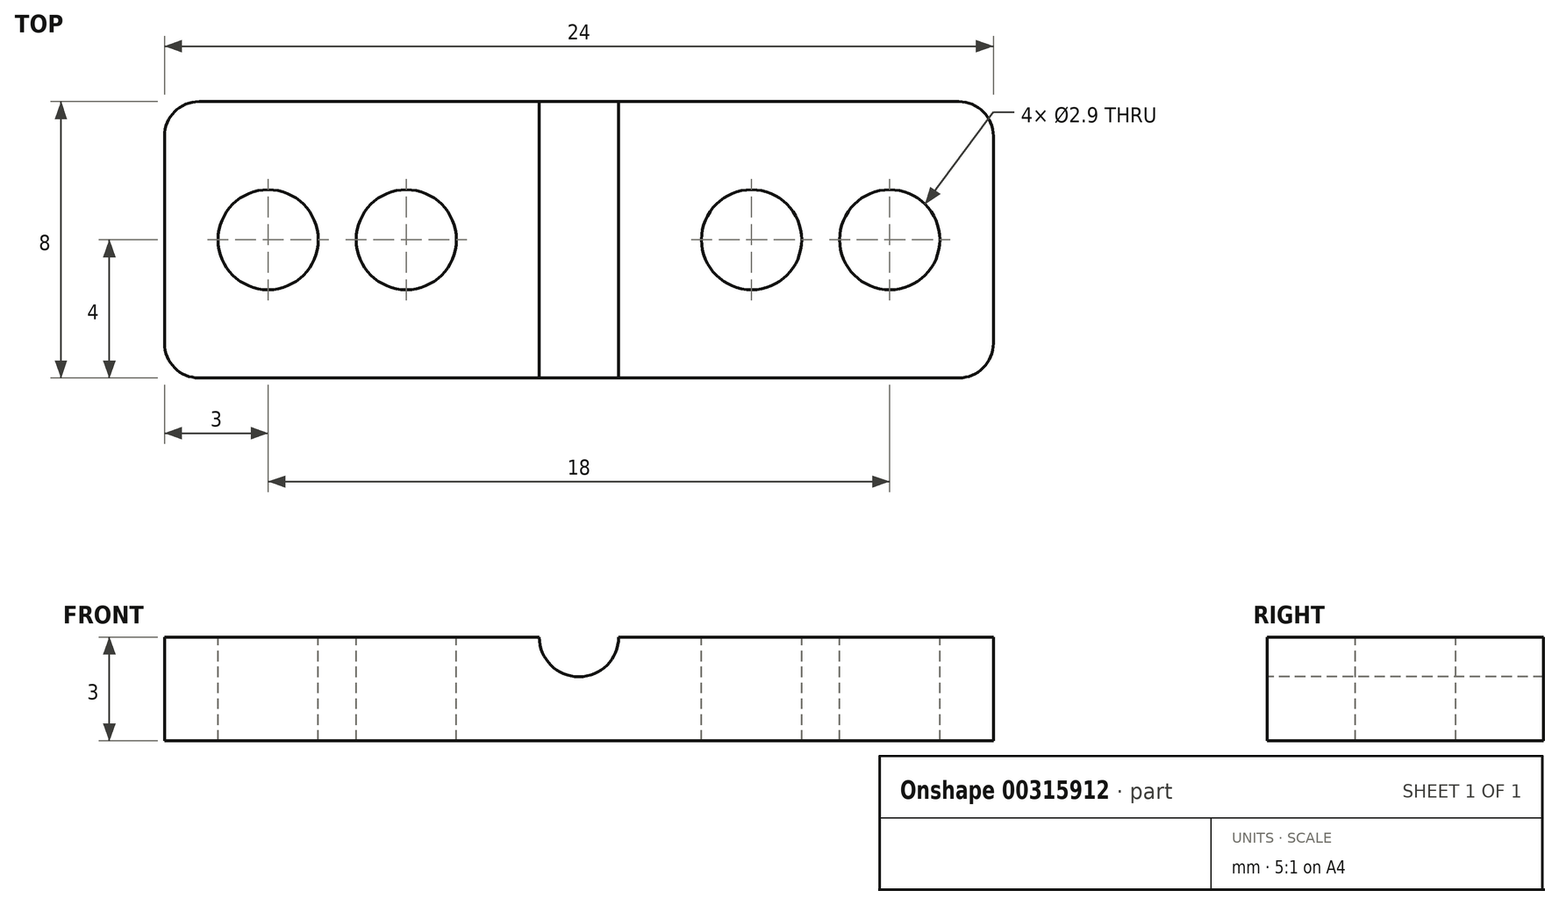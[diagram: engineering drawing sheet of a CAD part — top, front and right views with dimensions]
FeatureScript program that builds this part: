
annotation { "Feature Type Name" : "Feature", "Feature Type Description" : "" }
export const myFeature = defineFeature(function(context is Context, id is Id, definition is map)
    precondition{}
    {
        {
            var Q0;
            Q0=qCreatedBy(makeId("Top.planeOp"),FACE);
            var sketch = newSketch(context, id + "F0", { "sketchPlane" : qUnion([Q0])});
            skLineSegment(sketch, "E0.bottom", {"start": v(3, 4) * mm, "end": v(-3, 4) * mm});
            skLineSegment(sketch, "E0.top", {"start": v(3, -4) * mm, "end": v(-3, -4) * mm});
            skLineSegment(sketch, "E0.left", {"start": v(3, 4) * mm, "end": v(3, -4) * mm});
            skLineSegment(sketch, "E0.right", {"start": v(-3, 4) * mm, "end": v(-3, -4) * mm});
            skPoint(sketch, "E0.middle", {"position": v(0, 0) * mm});
            skLineSegment(sketch, "E1.bottom", {"start": v(21, 4) * mm, "end": v(15, 4) * mm});
            skLineSegment(sketch, "E1.top", {"start": v(21, -4) * mm, "end": v(15, -4) * mm});
            skLineSegment(sketch, "E1.left", {"start": v(21, 4) * mm, "end": v(21, -4) * mm});
            skLineSegment(sketch, "E1.right", {"start": v(15, 4) * mm, "end": v(15, -4) * mm});
            skPoint(sketch, "E1.middle", {"position": v(18, 0) * mm});
            skLineSegment(sketch, "E2", {"start": v(3, 4) * mm, "end": v(15, 4) * mm});
            skLineSegment(sketch, "E3", {"start": v(3, -4) * mm, "end": v(15, -4) * mm});
            skLineSegment(sketch, "E4", {"start": v(9, 4) * mm, "end": v(9, -4) * mm, "construction": true});
            skLineSegment(sketch, "E5.direction1", {"start": v(9, -4) * mm, "end": v(15, -4) * mm, "construction": true});
            skPoint(sketch, "E6", {"position": v(4, 0) * mm});
            skPoint(sketch, "E6.positionSnap0", {"position": v(3, 0) * mm});
            skPoint(sketch, "E7", {"position": v(14, 0) * mm});
            skPoint(sketch, "E7.positionSnap0", {"position": v(15, 0) * mm});
            skSolve(sketch);
        }
        {
            var Q0;
            Q0=makeQuery(id+"F0.imprint","IMPRINT",FACE,{"disambiguationData":[TD([[makeQuery(id+"F0.imprint","IMPRINT",EDGE,{"derivedFrom":sQuery(id+"F0.wireOp",EDGE,"E0.bottom")}),1.0]])]});
            var Q1;
            Q1=makeQuery(id+"F0.imprint","IMPRINT",FACE,{"disambiguationData":[TD([[makeQuery(id+"F0.imprint","IMPRINT",EDGE,{"derivedFrom":sQuery(id+"F0.wireOp",EDGE,"E0.left")}),1.0]])]});
            var Q2;
            Q2=makeQuery(id+"F0.imprint","IMPRINT",FACE,{"disambiguationData":[TD([[makeQuery(id+"F0.imprint","IMPRINT",EDGE,{"derivedFrom":sQuery(id+"F0.wireOp",EDGE,"E1.bottom")}),1.0]])]});
            extrude(context, id + "F1", {"entities" : qUnion([Q0, Q1, Q2]), "oppositeDirection" : true, "depth" : 3 * mm});
        }
        {
            var Q0;
            Q0=sQuery(id+"F0.wireOp",VERTEX,"E0.middle");
            var Q1;
            Q1=sQuery(id+"F0.wireOp",VERTEX,"E6");
            var Q2;
            Q2=sQuery(id+"F0.wireOp",VERTEX,"E7");
            var Q3;
            Q3=sQuery(id+"F0.wireOp",VERTEX,"E1.middle");
            var Q4;
            Q4=makeQuery(id+"F1.opExtrude","SWEPT_BODY",BODY,{"disambiguationData":[OSD([sQuery(id+"F0.wireOp",EDGE,"E0.bottom"),sQuery(id+"F0.wireOp",EDGE,"E0.top"),sQuery(id+"F0.wireOp",EDGE,"E0.right"),sQuery(id+"F0.wireOp",EDGE,"E1.bottom"),sQuery(id+"F0.wireOp",EDGE,"E1.top"),sQuery(id+"F0.wireOp",EDGE,"E1.left"),sQuery(id+"F0.wireOp",EDGE,"E2"),sQuery(id+"F0.wireOp",EDGE,"E3")])]});
            hole(context, id + "F2", {"style" : HoleStyle.SIMPLE, "endStyle" : HoleEndStyle.THROUGH, "holeDiameter" : 2.9 * mm, "tappedDepth" : 12 * mm, "tapClearance" : 3, "locations" : qUnion([Q0, Q1, Q2, Q3]), "scope" : qUnion([Q4])});
        }
        {
            var Q0;
            {var subQ0=sQuery(id+"F0.wireOp",EDGE,"E3");var subQ1=sQuery(id+"F0.wireOp",EDGE,"E1.top");var subQ2=sQuery(id+"F0.wireOp",EDGE,"E0.top");Q0=makeQuery(id+"FaaVOSY5iOmgxNq_1.boolean.opBoolean","MERGE",FACE,{"derivedFrom":[makeQuery(id+"F1.opExtrude","SWEPT_FACE",FACE,{"disambiguationData":[OSD([subQ2,subQ1,subQ0])]}),makeQuery(id+"FaaVOSY5iOmgxNq_1.opExtrude","SWEPT_FACE",FACE,{"disambiguationData":[OSD([subQ2,subQ1,subQ0])]})]});}
            var sketch = newSketch(context, id + "F3", { "sketchPlane" : qUnion([Q0])});
            skPoint(sketch, "E8", {"position": v(9, 0) * mm});
            skLineSegment(sketch, "E9.direction1", {"start": v(9, 0) * mm, "end": v(15, 0) * mm, "construction": true});
            skSolve(sketch);
        }
        {
            var Q0;
            Q0=sQuery(id+"F3.wireOp",VERTEX,"E8");
            var Q1;
            Q1=makeQuery(id+"F1.opExtrude","SWEPT_BODY",BODY,{"disambiguationData":[OSD([sQuery(id+"F0.wireOp",EDGE,"E0.bottom"),sQuery(id+"F0.wireOp",EDGE,"E0.top"),sQuery(id+"F0.wireOp",EDGE,"E0.right"),sQuery(id+"F0.wireOp",EDGE,"E1.bottom"),sQuery(id+"F0.wireOp",EDGE,"E1.top"),sQuery(id+"F0.wireOp",EDGE,"E1.left"),sQuery(id+"F0.wireOp",EDGE,"E2"),sQuery(id+"F0.wireOp",EDGE,"E3")])]});
            hole(context, id + "F4", {"style" : HoleStyle.SIMPLE, "endStyle" : HoleEndStyle.THROUGH, "holeDiameter" : 2.3 * mm, "tappedDepth" : 12 * mm, "tapClearance" : 3, "locations" : qUnion([Q0]), "scope" : qUnion([Q1])});
        }
        {
            var Q0;
            Q0=makeQuery(id+"F1.opExtrude","SWEPT_EDGE",EDGE,{"disambiguationData":[OSD([sQuery(id+"F0.wireOp",EDGE,"E0.top"),sQuery(id+"F0.wireOp",EDGE,"E0.right")])]});
            var Q1;
            Q1=makeQuery(id+"F1.opExtrude","SWEPT_EDGE",EDGE,{"disambiguationData":[OSD([sQuery(id+"F0.wireOp",EDGE,"E1.top"),sQuery(id+"F0.wireOp",EDGE,"E1.left")])]});
            var Q2;
            Q2=makeQuery(id+"F1.opExtrude","SWEPT_EDGE",EDGE,{"disambiguationData":[OSD([sQuery(id+"F0.wireOp",EDGE,"E1.bottom"),sQuery(id+"F0.wireOp",EDGE,"E1.left")])]});
            var Q3;
            Q3=makeQuery(id+"F1.opExtrude","SWEPT_EDGE",EDGE,{"disambiguationData":[OSD([sQuery(id+"F0.wireOp",EDGE,"E0.bottom"),sQuery(id+"F0.wireOp",EDGE,"E0.right")])]});
            fillet(context, id + "F5", {"entities" : qUnion([Q0, Q1, Q2, Q3]), "radius" : 1 * mm, "tangentPropagation" : true, "allowEdgeOverflow" : false});
        }
    });
